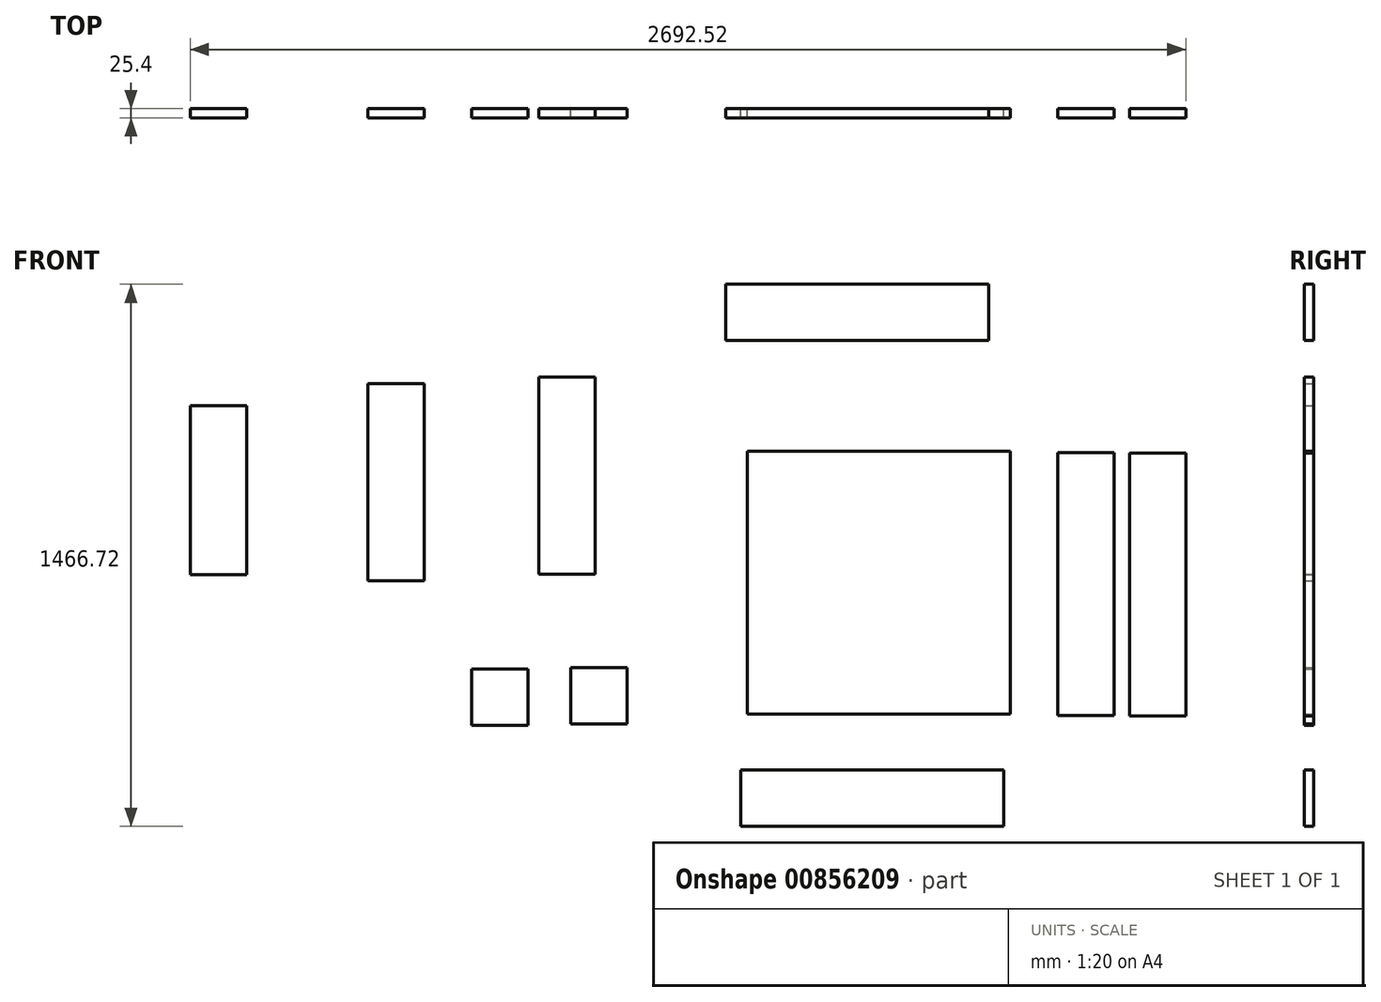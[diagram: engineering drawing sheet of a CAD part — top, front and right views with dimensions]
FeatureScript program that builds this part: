
annotation { "Feature Type Name" : "Feature", "Feature Type Description" : "" }
export const myFeature = defineFeature(function(context is Context, id is Id, definition is map)
    precondition{}
    {
        {
            var Q0;
            Q0=qCreatedBy(makeId("Front.planeOp"),FACE);
            var sketch = newSketch(context, id + "F0", { "sketchPlane" : qUnion([Q0])});
            skLineSegment(sketch, "E0.bottom", {"start": v(-392.84, 513.4) * mm, "end": v(318.36, 513.4) * mm});
            skLineSegment(sketch, "E0.top", {"start": v(-392.84, -197.8) * mm, "end": v(318.36, -197.8) * mm});
            skLineSegment(sketch, "E0.left", {"start": v(-392.84, 513.4) * mm, "end": v(-392.84, -197.8) * mm});
            skLineSegment(sketch, "E0.right", {"start": v(318.36, 513.4) * mm, "end": v(318.36, -197.8) * mm});
            skLineSegment(sketch, "E1.bottom", {"start": v(447.23, 509.8) * mm, "end": v(599.63, 509.8) * mm});
            skLineSegment(sketch, "E1.top", {"start": v(447.23, -201.4) * mm, "end": v(599.63, -201.4) * mm});
            skLineSegment(sketch, "E1.left", {"start": v(447.23, 509.8) * mm, "end": v(447.23, -201.4) * mm});
            skLineSegment(sketch, "E1.right", {"start": v(599.63, 509.8) * mm, "end": v(599.63, -201.4) * mm});
            skLineSegment(sketch, "E2.bottom", {"start": v(640.83, 508.71) * mm, "end": v(793.23, 508.71) * mm});
            skLineSegment(sketch, "E2.top", {"start": v(640.83, -202.49) * mm, "end": v(793.23, -202.49) * mm});
            skLineSegment(sketch, "E2.left", {"start": v(640.83, 508.71) * mm, "end": v(640.83, -202.49) * mm});
            skLineSegment(sketch, "E2.right", {"start": v(793.23, 508.71) * mm, "end": v(793.23, -202.49) * mm});
            skLineSegment(sketch, "E3.bottom", {"start": v(-450.54, 965.52) * mm, "end": v(260.66, 965.52) * mm});
            skLineSegment(sketch, "E3.top", {"start": v(-450.54, 813.12) * mm, "end": v(260.66, 813.12) * mm});
            skLineSegment(sketch, "E3.left", {"start": v(-450.54, 965.52) * mm, "end": v(-450.54, 813.12) * mm});
            skLineSegment(sketch, "E3.right", {"start": v(260.66, 965.52) * mm, "end": v(260.66, 813.12) * mm});
            skLineSegment(sketch, "E4.bottom", {"start": v(-410.7, -348.8) * mm, "end": v(300.5, -348.8) * mm});
            skLineSegment(sketch, "E4.top", {"start": v(-410.7, -501.2) * mm, "end": v(300.5, -501.2) * mm});
            skLineSegment(sketch, "E4.left", {"start": v(-410.7, -348.8) * mm, "end": v(-410.7, -501.2) * mm});
            skLineSegment(sketch, "E4.right", {"start": v(300.5, -348.8) * mm, "end": v(300.5, -501.2) * mm});
            skLineSegment(sketch, "E5.bottom", {"start": v(-956.89, 714.3) * mm, "end": v(-804.49, 714.3) * mm});
            skLineSegment(sketch, "E5.top", {"start": v(-956.89, 180.9) * mm, "end": v(-804.49, 180.9) * mm});
            skLineSegment(sketch, "E5.left", {"start": v(-956.89, 714.3) * mm, "end": v(-956.89, 180.9) * mm});
            skLineSegment(sketch, "E5.right", {"start": v(-804.49, 714.3) * mm, "end": v(-804.49, 180.9) * mm});
            skLineSegment(sketch, "E6.bottom", {"start": v(-1418.46, 696.34) * mm, "end": v(-1266.06, 696.34) * mm});
            skLineSegment(sketch, "E6.top", {"start": v(-1418.46, 162.94) * mm, "end": v(-1266.06, 162.94) * mm});
            skLineSegment(sketch, "E6.left", {"start": v(-1418.46, 696.34) * mm, "end": v(-1418.46, 162.94) * mm});
            skLineSegment(sketch, "E6.right", {"start": v(-1266.06, 696.34) * mm, "end": v(-1266.06, 162.94) * mm});
            skLineSegment(sketch, "E7.bottom", {"start": v(-870.3, -71.97) * mm, "end": v(-717.9, -71.97) * mm});
            skLineSegment(sketch, "E7.top", {"start": v(-870.3, -224.37) * mm, "end": v(-717.9, -224.37) * mm});
            skLineSegment(sketch, "E7.left", {"start": v(-870.3, -71.97) * mm, "end": v(-870.3, -224.37) * mm});
            skLineSegment(sketch, "E7.right", {"start": v(-717.9, -71.97) * mm, "end": v(-717.9, -224.37) * mm});
            skLineSegment(sketch, "E8.bottom", {"start": v(-1138.65, -75.02) * mm, "end": v(-986.25, -75.02) * mm});
            skLineSegment(sketch, "E8.top", {"start": v(-1138.65, -227.42) * mm, "end": v(-986.25, -227.42) * mm});
            skLineSegment(sketch, "E8.left", {"start": v(-1138.65, -75.02) * mm, "end": v(-1138.65, -227.42) * mm});
            skLineSegment(sketch, "E8.right", {"start": v(-986.25, -75.02) * mm, "end": v(-986.25, -227.42) * mm});
            skLineSegment(sketch, "E9.bottom", {"start": v(-1899.29, 636.93) * mm, "end": v(-1746.89, 636.93) * mm});
            skLineSegment(sketch, "E9.top", {"start": v(-1899.29, 179.73) * mm, "end": v(-1746.89, 179.73) * mm});
            skLineSegment(sketch, "E9.left", {"start": v(-1899.29, 636.93) * mm, "end": v(-1899.29, 179.73) * mm});
            skLineSegment(sketch, "E9.right", {"start": v(-1746.89, 636.93) * mm, "end": v(-1746.89, 179.73) * mm});
            skSolve(sketch);
        }
        {
            var Q0;
            Q0=makeQuery(id+"F0.imprint","IMPRINT",FACE,{"disambiguationData":[TD([[makeQuery(id+"F0.imprint","IMPRINT",EDGE,{"derivedFrom":sQuery(id+"F0.wireOp",EDGE,"E9.bottom")}),-1.0]])]});
            var Q1;
            Q1=makeQuery(id+"F0.imprint","IMPRINT",FACE,{"disambiguationData":[TD([[makeQuery(id+"F0.imprint","IMPRINT",EDGE,{"derivedFrom":sQuery(id+"F0.wireOp",EDGE,"E6.bottom")}),-1.0]])]});
            var Q2;
            Q2=makeQuery(id+"F0.imprint","IMPRINT",FACE,{"disambiguationData":[TD([[makeQuery(id+"F0.imprint","IMPRINT",EDGE,{"derivedFrom":sQuery(id+"F0.wireOp",EDGE,"E5.bottom")}),-1.0]])]});
            var Q3;
            Q3=makeQuery(id+"F0.imprint","IMPRINT",FACE,{"disambiguationData":[TD([[makeQuery(id+"F0.imprint","IMPRINT",EDGE,{"derivedFrom":sQuery(id+"F0.wireOp",EDGE,"E3.bottom")}),-1.0]])]});
            var Q4;
            Q4=makeQuery(id+"F0.imprint","IMPRINT",FACE,{"disambiguationData":[TD([[makeQuery(id+"F0.imprint","IMPRINT",EDGE,{"derivedFrom":sQuery(id+"F0.wireOp",EDGE,"E0.bottom")}),-1.0]])]});
            var Q5;
            Q5=makeQuery(id+"F0.imprint","IMPRINT",FACE,{"disambiguationData":[TD([[makeQuery(id+"F0.imprint","IMPRINT",EDGE,{"derivedFrom":sQuery(id+"F0.wireOp",EDGE,"E4.bottom")}),-1.0]])]});
            var Q6;
            Q6=makeQuery(id+"F0.imprint","IMPRINT",FACE,{"disambiguationData":[TD([[makeQuery(id+"F0.imprint","IMPRINT",EDGE,{"derivedFrom":sQuery(id+"F0.wireOp",EDGE,"E7.bottom")}),-1.0]])]});
            var Q7;
            Q7=makeQuery(id+"F0.imprint","IMPRINT",FACE,{"disambiguationData":[TD([[makeQuery(id+"F0.imprint","IMPRINT",EDGE,{"derivedFrom":sQuery(id+"F0.wireOp",EDGE,"E8.bottom")}),-1.0]])]});
            var Q8;
            Q8=makeQuery(id+"F0.imprint","IMPRINT",FACE,{"disambiguationData":[TD([[makeQuery(id+"F0.imprint","IMPRINT",EDGE,{"derivedFrom":sQuery(id+"F0.wireOp",EDGE,"E1.bottom")}),-1.0]])]});
            var Q9;
            Q9=makeQuery(id+"F0.imprint","IMPRINT",FACE,{"disambiguationData":[TD([[makeQuery(id+"F0.imprint","IMPRINT",EDGE,{"derivedFrom":sQuery(id+"F0.wireOp",EDGE,"E2.bottom")}),-1.0]])]});
            extrude(context, id + "F1", {"entities" : qUnion([Q0, Q1, Q2, Q3, Q4, Q5, Q6, Q7, Q8, Q9]), "depth" : 25.4 * mm, "offsetDistance" : 25.4 * mm});
        }
    });
